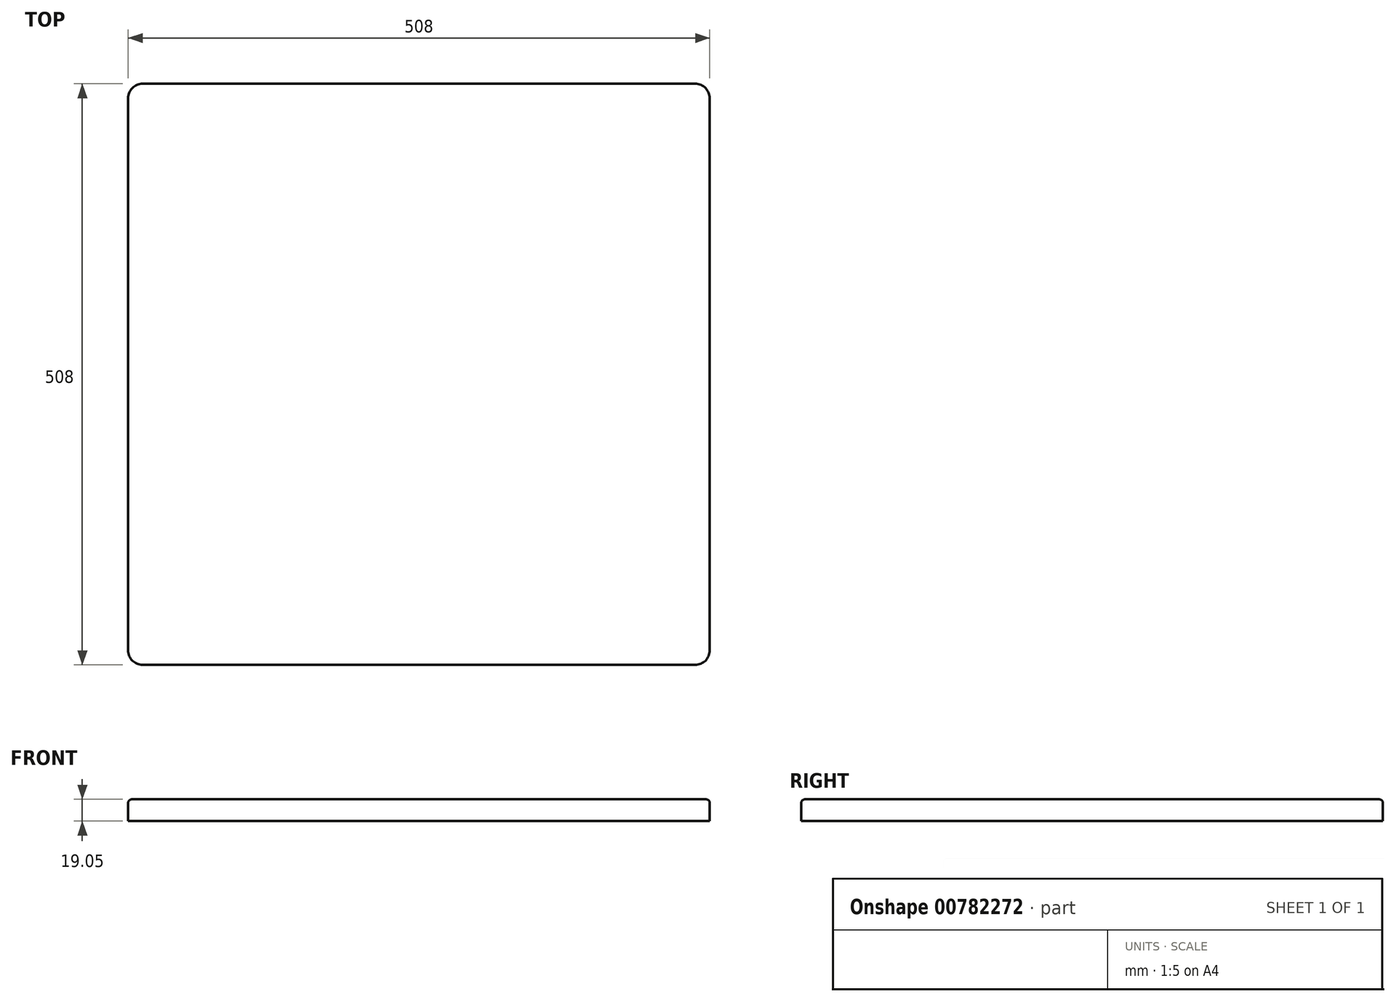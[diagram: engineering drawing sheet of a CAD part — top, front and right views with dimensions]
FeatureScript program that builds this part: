
annotation { "Feature Type Name" : "Feature", "Feature Type Description" : "" }
export const myFeature = defineFeature(function(context is Context, id is Id, definition is map)
    precondition{}
    {
        {
            var Q0;
            Q0=qCreatedBy(makeId("Top.planeOp"),FACE);
            var sketch = newSketch(context, id + "F0", { "sketchPlane" : qUnion([Q0])});
            skLineSegment(sketch, "E0.bottom", {"start": v(-254, 254) * mm, "end": v(254, 254) * mm});
            skLineSegment(sketch, "E0.top", {"start": v(-254, -254) * mm, "end": v(254, -254) * mm});
            skLineSegment(sketch, "E0.left", {"start": v(-254, 254) * mm, "end": v(-254, -254) * mm});
            skLineSegment(sketch, "E0.right", {"start": v(254, 254) * mm, "end": v(254, -254) * mm});
            skLineSegment(sketch, "E1", {"start": v(-254, 254) * mm, "end": v(254, -254) * mm, "construction": true});
            skSolve(sketch);
        }
        {
            var Q0;
            Q0=makeQuery(id+"F0.imprint","IMPRINT",FACE,{"disambiguationData":[TD([[makeQuery(id+"F0.imprint","IMPRINT",EDGE,{"derivedFrom":sQuery(id+"F0.wireOp",EDGE,"E0.bottom")}),-1.0]])]});
            extrude(context, id + "F1", {"entities" : qUnion([Q0]), "depth" : 19.05 * mm, "offsetDistance" : 25.4 * mm});
        }
        {
            var Q0;
            Q0=makeQuery(id+"F1.opExtrude","SWEPT_EDGE",EDGE,{"disambiguationData":[OSD([sQuery(id+"F0.wireOp",EDGE,"E0.bottom"),sQuery(id+"F0.wireOp",EDGE,"E0.left")])]});
            var Q1;
            Q1=makeQuery(id+"F1.opExtrude","SWEPT_EDGE",EDGE,{"disambiguationData":[OSD([sQuery(id+"F0.wireOp",EDGE,"E0.bottom"),sQuery(id+"F0.wireOp",EDGE,"E0.right")])]});
            var Q2;
            Q2=makeQuery(id+"F1.opExtrude","SWEPT_EDGE",EDGE,{"disambiguationData":[OSD([sQuery(id+"F0.wireOp",EDGE,"E0.top"),sQuery(id+"F0.wireOp",EDGE,"E0.left")])]});
            var Q3;
            Q3=makeQuery(id+"F1.opExtrude","SWEPT_EDGE",EDGE,{"disambiguationData":[OSD([sQuery(id+"F0.wireOp",EDGE,"E0.top"),sQuery(id+"F0.wireOp",EDGE,"E0.right")])]});
            fillet(context, id + "F2", {"entities" : qUnion([Q0, Q1, Q2, Q3]), "radius" : 12.7 * mm, "tangentPropagation" : true, "allowEdgeOverflow" : false});
        }
        {
            var Q0;
            Q0=makeQuery(id+"F1.opExtrude","CAP_EDGE",EDGE,{"disambiguationData":[OSD([sQuery(id+"F0.wireOp",EDGE,"E0.left")])],"isStart":false});
            fillet(context, id + "F3", {"entities" : qUnion([Q0]), "radius" : 3.17 * mm, "tangentPropagation" : true, "allowEdgeOverflow" : false});
        }
    });
